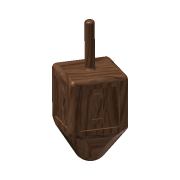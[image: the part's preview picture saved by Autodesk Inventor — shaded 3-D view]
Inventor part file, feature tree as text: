
AUTODESK INVENTOR PART (.ipt)
format: ipt  version: 2013 SP2 (Build 170200200, 200)  size: 420,864 bytes
history: native  units: in
note: dims shown in document units (in); Inventor stores cm internally (conversion verified against a paired STEP export)
features: extrude x11, sketch x11, projected_geometry x8, fillet x4
ambient origin geometry x8: Origin, YZ Plane, XZ Plane, XY Plane, X Axis, Y Axis, Z Axis, Center Point
bodies: Solid1 (feature_tree)
feature tree (34):
  extrude  "Extrusion1"  Depth=1.5in
  extrude  "Extrusion2"  Depth=0.25in
  extrude  "Extrusion3"  Depth=1.3125in
  fillet  "Fillet1"  Radius=0.4375in
  fillet  "Fillet2"  Radius=0.125in
  fillet  "Fillet3"  Radius=0.125in
  fillet  "Fillet4"  Radius=0.0625in
  extrude  "Extrusion4"  Depth=0.125in
  extrude  "Extrusion5"  Depth=0.125in
  extrude  "Extrusion6"  Depth=0.0625in TaperAngle=0.0deg
  extrude  "Extrusion7"  Depth=0.125in
  extrude  "Extrusion8"  Depth=0.125in
  extrude  "Extrusion9"  Depth=0.0625in TaperAngle=0.0deg
  extrude  "Extrusion10"  Depth=0.0625in TaperAngle=0.0deg
  extrude  "Extrusion11"  Depth=0.0625in TaperAngle=0.0deg
  sketch  "Sketch1"  dims[d0=1.5in d1=1.5in]
  sketch  "Sketch2"  dims[d2=1.5in d3=0.0in d4=0.25in]
  sketch  "Sketch3"  dims[d5=1.25in d6=0.0in d7=1.3125in d8=-0.2061in d9=0.4375in d10=0.25in d11=0.125in d12=0.125in d13=0.0625in]
  projected_geometry  "Projected Loop1"
  sketch  "Sketch4"  dims[d14=0.125in d15=0.125in]
  projected_geometry  "Projected Loop2"
  sketch  "Sketch5"  dims[d16=0.125in d17=0.125in]
  projected_geometry  "Projected Loop3"
  sketch  "Sketch6"  dims[d18=0.125in d19=0.0625in d20=0.0in]
  projected_geometry  "Projected Loop4"
  sketch  "Sketch7"  dims[d21=0.0625in d22=0.0in d23=0.125in]
  projected_geometry  "Projected Loop5"
  sketch  "Sketch8"  dims[d24=0.125in d25=0.125in]
  projected_geometry  "Projected Loop6"
  sketch  "Sketch9"  dims[d26=0.125in d27=0.0625in d28=0.0in]
  projected_geometry  "Projected Loop7"
  sketch  "Sketch10"  dims[d29=0.0625in d30=0.0in d31=0.0625in d32=0.0in]
  sketch  "Sketch11"  dims[d33=0.0625in d34=0.0in d35=0.0625in d36=0.0in d37=0.0625in d38=0.0in]
  projected_geometry  "Projected Loop8"
